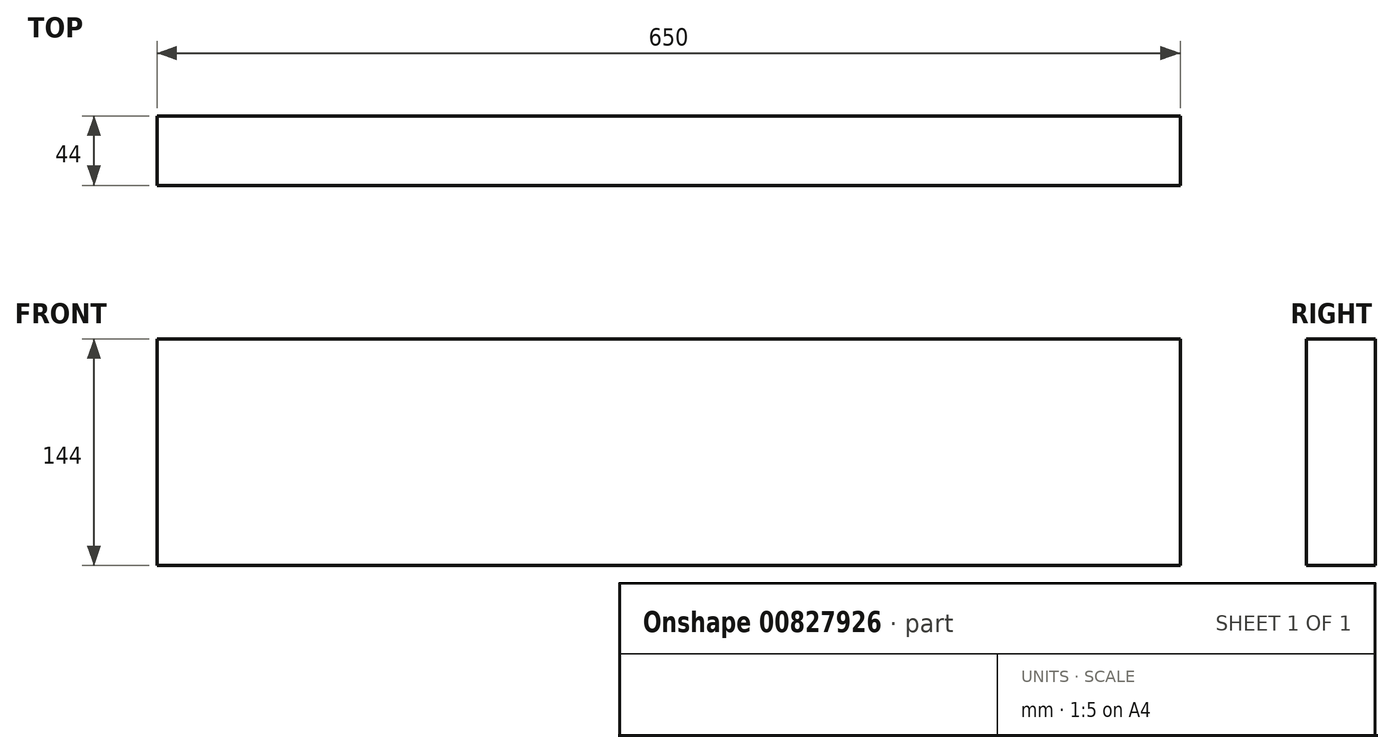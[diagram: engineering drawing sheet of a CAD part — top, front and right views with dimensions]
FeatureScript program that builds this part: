
annotation { "Feature Type Name" : "Feature", "Feature Type Description" : "" }
export const myFeature = defineFeature(function(context is Context, id is Id, definition is map)
    precondition{}
    {
        {
            var Q0;
            Q0=qCreatedBy(makeId("Top.planeOp"),FACE);
            var sketch = newSketch(context, id + "F0", { "sketchPlane" : qUnion([Q0])});
            skLineSegment(sketch, "E0.bottom", {"start": v(-325, 22) * mm, "end": v(325, 22) * mm});
            skLineSegment(sketch, "E0.top", {"start": v(-325, -22) * mm, "end": v(325, -22) * mm});
            skLineSegment(sketch, "E0.left", {"start": v(-325, 22) * mm, "end": v(-325, -22) * mm});
            skLineSegment(sketch, "E0.right", {"start": v(325, 22) * mm, "end": v(325, -22) * mm});
            skPoint(sketch, "E0.middle", {"position": v(0, 0) * mm});
            skSolve(sketch);
        }
        {
            var Q0;
            Q0=makeQuery(id+"F0.imprint","IMPRINT",FACE,{"disambiguationData":[TD([[makeQuery(id+"F0.imprint","IMPRINT",EDGE,{"derivedFrom":sQuery(id+"F0.wireOp",EDGE,"E0.bottom")}),-1.0]])]});
            extrude(context, id + "F1", {"entities" : qUnion([Q0]), "depth" : 144 * mm, "offsetDistance" : 25 * mm});
        }
    });
